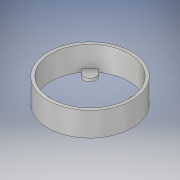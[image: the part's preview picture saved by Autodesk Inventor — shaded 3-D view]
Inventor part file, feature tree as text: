
AUTODESK INVENTOR PART (.ipt)
format: ipt  version: 2017 (Build 210142000, 142)  size: 137,216 bytes
history: native  units: in
note: dims shown in document units (in); Inventor stores cm internally (conversion verified against a paired STEP export)
features: extrude x2, sketch x2
ambient origin geometry x8: Origin, YZ Plane, XZ Plane, XY Plane, X Axis, Y Axis, Z Axis, Center Point
bodies: Solid1 (feature_tree)
feature tree (4):
  extrude  "Extrusion1"  Depth=7.0in
  extrude  "Extrusion2"  Depth=1.0in
  sketch  "Sketch1"  dims[d0=6.5in d1=7.0in]
  sketch  "Sketch2"  dims[d2=2.0in d3=0.0in d4=1.0in d7=0.25in d8=0.0in]
